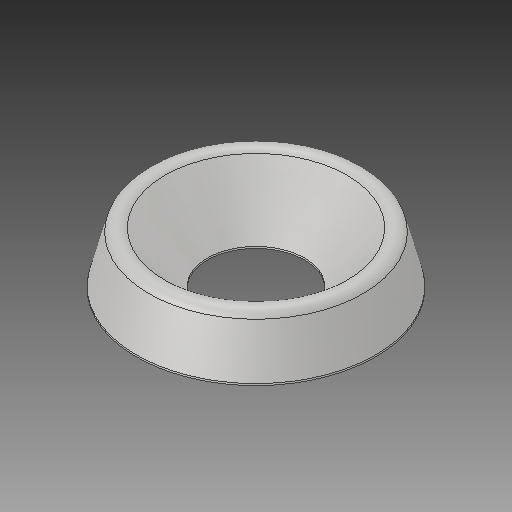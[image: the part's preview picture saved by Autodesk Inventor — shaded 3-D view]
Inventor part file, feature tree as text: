
AUTODESK INVENTOR PART (.ipt)
format: ipt  version: 2019 (Build 230136000, 136)  size: 160,768 bytes
history: mixed  units: mm
features: shell x1, imported_body x1
ambient origin geometry x8: Origin, YZ Plane, XZ Plane, XY Plane, X Axis, Y Axis, Z Axis, Center Point
bodies: Solid1 (imported_parasolid)
feature tree (2):
  shell  "Shell2"  [1 undecoded]
  imported_body  NMx_Import_Brep_tag  [imported B-rep: ~10 faces, bbox_mm=[0.0, 3.822048, 16.68145]]
note: 1 required parameter value undecoded (feature->parameter linkage not recoverable at this tier; creation-order binding heuristic only, values carry confidence <= 0.55)
